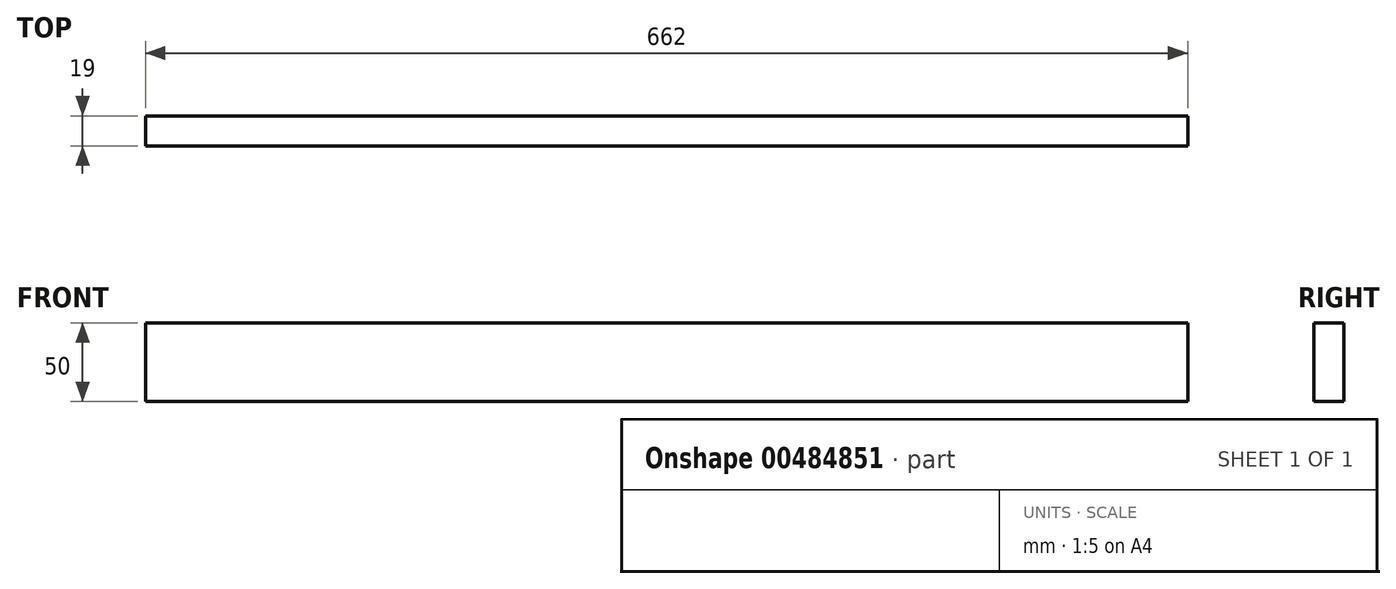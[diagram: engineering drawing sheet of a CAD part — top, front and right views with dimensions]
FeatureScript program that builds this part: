
annotation { "Feature Type Name" : "Feature", "Feature Type Description" : "" }
export const myFeature = defineFeature(function(context is Context, id is Id, definition is map)
    precondition{}
    {
        {
            var Q0;
            Q0=qCreatedBy(makeId("Front.planeOp"),FACE);
            var sketch = newSketch(context, id + "F0", { "sketchPlane" : qUnion([Q0])});
            skLineSegment(sketch, "E0.bottom", {"start": v(-125.95, 55.15) * mm, "end": v(536.05, 55.15) * mm});
            skLineSegment(sketch, "E0.top", {"start": v(-125.95, 5.15) * mm, "end": v(536.05, 5.15) * mm});
            skLineSegment(sketch, "E0.left", {"start": v(-125.95, 55.15) * mm, "end": v(-125.95, 5.15) * mm});
            skLineSegment(sketch, "E0.right", {"start": v(536.05, 55.15) * mm, "end": v(536.05, 5.15) * mm});
            skSolve(sketch);
        }
        {
            var Q0;
            Q0=makeQuery(id+"F0.imprint","IMPRINT",FACE,{"disambiguationData":[TD([[makeQuery(id+"F0.imprint","IMPRINT",EDGE,{"derivedFrom":sQuery(id+"F0.wireOp",EDGE,"E0.bottom")}),-1.0]])]});
            extrude(context, id + "F1", {"entities" : qUnion([Q0]), "depth" : 19 * mm});
        }
    });
